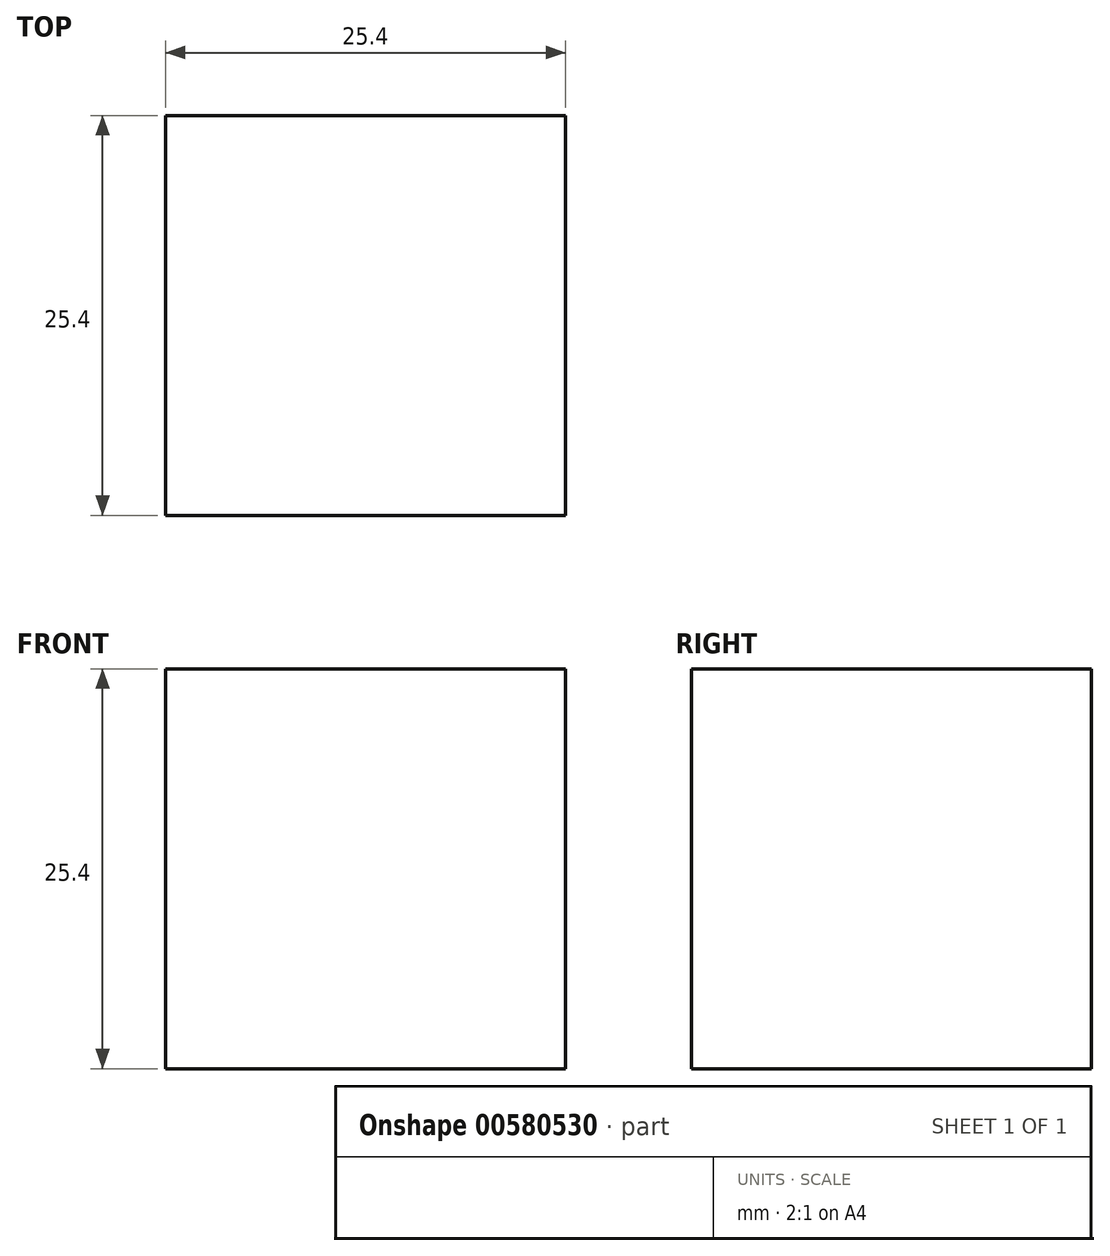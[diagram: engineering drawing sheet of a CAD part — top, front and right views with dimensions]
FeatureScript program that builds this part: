
annotation { "Feature Type Name" : "Feature", "Feature Type Description" : "" }
export const myFeature = defineFeature(function(context is Context, id is Id, definition is map)
    precondition{}
    {
        {
            var Q0;
            Q0=qCreatedBy(makeId("Front.planeOp"),FACE);
            var sketch = newSketch(context, id + "F0", { "sketchPlane" : qUnion([Q0])});
            skLineSegment(sketch, "E0.bottom", {"start": v(-12.7, 12.7) * mm, "end": v(12.7, 12.7) * mm});
            skLineSegment(sketch, "E0.top", {"start": v(-12.7, -12.7) * mm, "end": v(12.7, -12.7) * mm});
            skLineSegment(sketch, "E0.left", {"start": v(-12.7, 12.7) * mm, "end": v(-12.7, -12.7) * mm});
            skLineSegment(sketch, "E0.right", {"start": v(12.7, 12.7) * mm, "end": v(12.7, -12.7) * mm});
            skPoint(sketch, "E0.middle", {"position": v(0, 0) * mm});
            skSolve(sketch);
        }
        {
            var Q0;
            Q0=makeQuery(id+"F0.imprint","IMPRINT",FACE,{"disambiguationData":[TD([[makeQuery(id+"F0.imprint","IMPRINT",EDGE,{"derivedFrom":sQuery(id+"F0.wireOp",EDGE,"E0.bottom")}),-1.0]])]});
            extrude(context, id + "F1", {"entities" : qUnion([Q0]), "endBound" : BoundingType.SYMMETRIC, "depth" : 25.4 * mm, "offsetDistance" : 25.4 * mm});
        }
    });
